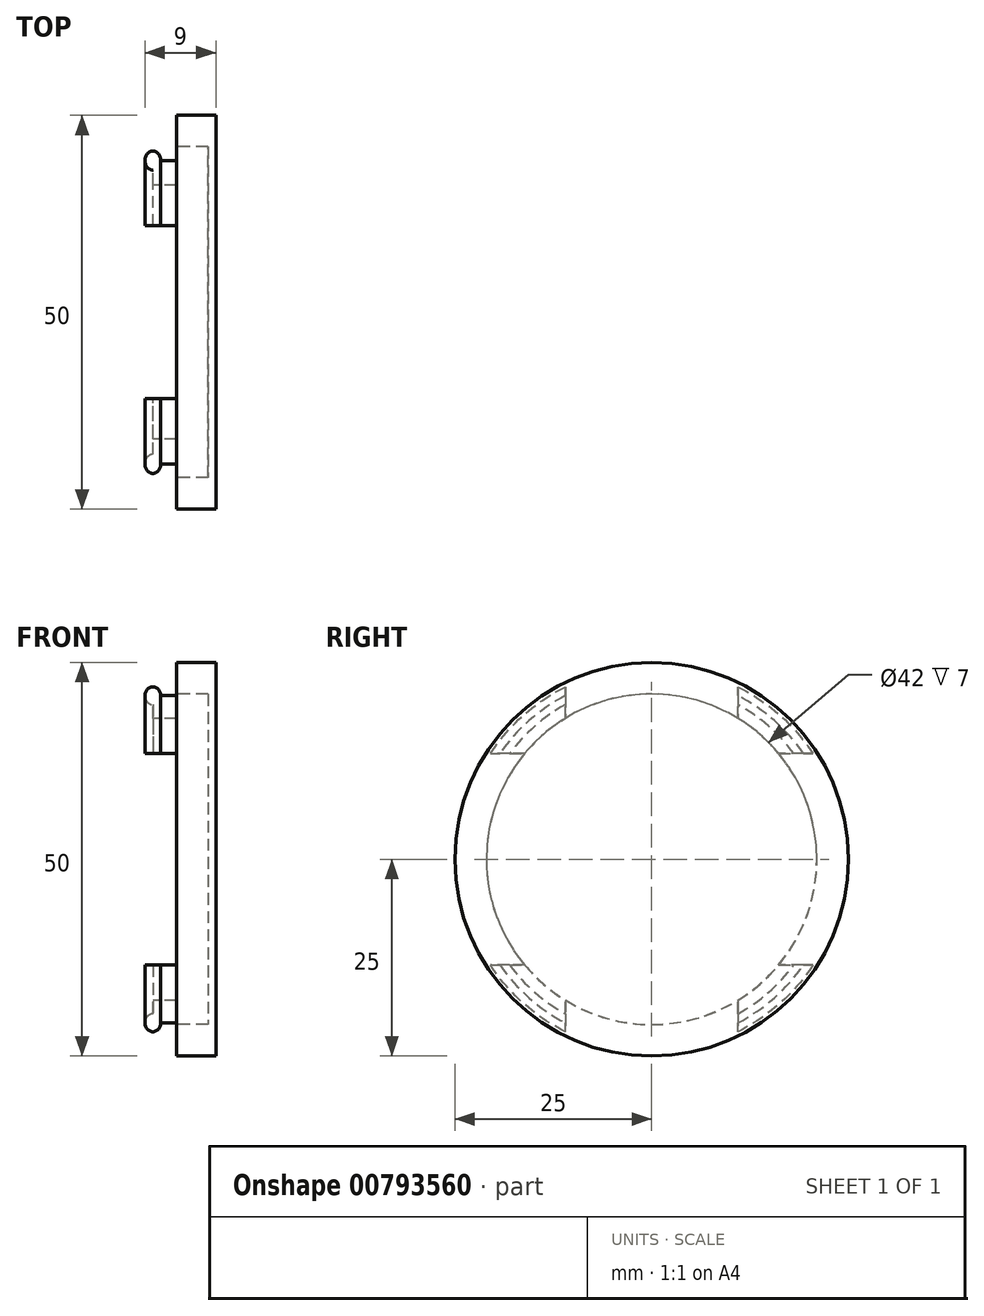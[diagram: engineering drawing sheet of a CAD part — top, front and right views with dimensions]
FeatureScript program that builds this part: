
annotation { "Feature Type Name" : "Feature", "Feature Type Description" : "" }
export const myFeature = defineFeature(function(context is Context, id is Id, definition is map)
    precondition{}
    {
        {
            var Q0;
            Q0=qCreatedBy(makeId("Top.planeOp"),FACE);
            var sketch = newSketch(context, id + "F0", { "sketchPlane" : qUnion([Q0])});
            skLineSegment(sketch, "E0.bottom", {"start": v(0, 25) * mm, "end": v(5, 25) * mm});
            skLineSegment(sketch, "E0.top", {"start": v(0, 0) * mm, "end": v(5, 0) * mm});
            skLineSegment(sketch, "E0.left", {"start": v(0, 25) * mm, "end": v(0, 0) * mm});
            skLineSegment(sketch, "E0.right", {"start": v(5, 25) * mm, "end": v(5, 0) * mm});
            skLineSegment(sketch, "E1.bottom", {"start": v(0, 0) * mm, "end": v(-3, 0) * mm});
            skLineSegment(sketch, "E1.top", {"start": v(0, 23.5) * mm, "end": v(-3, 23.5) * mm});
            skLineSegment(sketch, "E1.left", {"start": v(0, 0) * mm, "end": v(0, 23.5) * mm});
            skLineSegment(sketch, "E1.right", {"start": v(-3, 0) * mm, "end": v(-3, 23.5) * mm});
            skCircle(sketch, "E2", {"center": v(-3, 23.5) * mm, "radius": 1 * mm});
            skSolve(sketch);
        }
        {
            var Q0;
            {var subQ1=sQuery(id+"F0.wireOp",EDGE,"E1.bottom");Q0=makeQuery(id+"F0.imprint","IMPRINT",FACE,{"disambiguationData":[TD([[makeQuery(id+"F0.imprint","IMPRINT",EDGE,{"derivedFrom":subQ1}),-1.0]])]});}
            var Q1;
            {var subQ0=sQuery(id+"F0.wireOp",EDGE,"E1.right");var subQ1=sQuery(id+"F0.wireOp",EDGE,"E1.top");var subQ2=makeQuery(id+"F0.imprint","INTERSECT",VERTEX,{"derivedFrom":[subQ1,subQ0]});Q1=makeQuery(id+"F0.imprint","IMPRINT",FACE,{"disambiguationData":[TD([[makeQuery(id+"F0.imprint","IMPRINT",EDGE,{"disambiguationData":[TD([[subQ2,1.0]])],"derivedFrom":subQ1}),1.0]])]});}
            var Q2;
            Q2=makeQuery(id+"F0.imprint","IMPRINT",FACE,{"disambiguationData":[TD([[makeQuery(id+"F0.imprint","IMPRINT",EDGE,{"derivedFrom":sQuery(id+"F0.wireOp",EDGE,"E0.bottom")}),-1.0]])]});
            var Q3;
            {var subQ0=sQuery(id+"F0.wireOp",EDGE,"E1.right");var subQ1=sQuery(id+"F0.wireOp",EDGE,"E1.top");var subQ2=makeQuery(id+"F0.imprint","INTERSECT",VERTEX,{"derivedFrom":[subQ1,subQ0]});Q3=makeQuery(id+"F0.imprint","IMPRINT",FACE,{"disambiguationData":[TD([[makeQuery(id+"F0.imprint","IMPRINT",EDGE,{"disambiguationData":[TD([[subQ2,1.0]])],"derivedFrom":subQ1}),-1.0]])]});}
            var Q4;
            Q4=sQuery(id+"F0.wireOp",EDGE,"E0.top");
            revolve(context, id + "F1", {"surfaceOperationType" : NewSurfaceOperationType.NEW, "entities" : qUnion([Q0, Q1, Q2, Q3]), "axis" : qUnion([Q4]), "revolveType" : RevolveType.FULL});
        }
        {
            var Q0;
            Q0=makeQuery(id+"F1.opRevolve","SWEPT_FACE",FACE,{"disambiguationData":[OSD([sQuery(id+"F0.wireOp",EDGE,"E1.right")])]});
            var sketch = newSketch(context, id + "F2", { "sketchPlane" : qUnion([Q0])});
            skCircle(sketch, "E3", {"center": v(0, 0) * mm, "radius": 21 * mm});
            skSolve(sketch);
        }
        {
            var Q0;
            Q0 = qSketchRegion(id + "F2", true);
            extrude(context, id + "F3", {"entities" : qUnion([Q0]), "operationType" : NewBodyOperationType.REMOVE, "oppositeDirection" : true, "depth" : 7 * mm, "offsetDistance" : 25 * mm});
        }
        {
            var Q0;
            Q0=makeQuery(id+"F1.opRevolve","SWEPT_FACE",FACE,{"disambiguationData":[OSD([sQuery(id+"F0.wireOp",EDGE,"E0.left")])]});
            var sketch = newSketch(context, id + "F4", { "sketchPlane" : qUnion([Q0])});
            skLineSegment(sketch, "E4.bottom", {"start": v(-10.98, 25.57) * mm, "end": v(10.98, 25.57) * mm});
            skLineSegment(sketch, "E4.top", {"start": v(-10.98, -25.57) * mm, "end": v(10.98, -25.57) * mm});
            skLineSegment(sketch, "E4.left", {"start": v(-10.98, 25.57) * mm, "end": v(-10.98, -25.57) * mm});
            skLineSegment(sketch, "E4.right", {"start": v(10.98, 25.57) * mm, "end": v(10.98, -25.57) * mm});
            skPoint(sketch, "E4.middle", {"position": v(0, 0) * mm});
            skLineSegment(sketch, "E5.bottom", {"start": v(-29.04, 13.44) * mm, "end": v(29.04, 13.44) * mm});
            skLineSegment(sketch, "E5.top", {"start": v(-29.04, -13.44) * mm, "end": v(29.04, -13.44) * mm});
            skLineSegment(sketch, "E5.left", {"start": v(-29.04, 13.44) * mm, "end": v(-29.04, -13.44) * mm});
            skLineSegment(sketch, "E5.right", {"start": v(29.04, 13.44) * mm, "end": v(29.04, -13.44) * mm});
            skSolve(sketch);
        }
        {
            var Q0;
            Q0 = qSketchRegion(id + "F4", true);
            extrude(context, id + "F5", {"entities" : qUnion([Q0]), "operationType" : NewBodyOperationType.REMOVE, "depth" : 7 * mm, "offsetDistance" : 25 * mm});
        }
    });
